# Revit family: Diverter_Trim-Grohe-Concetto-29102_Series
name_source: partatom
category: Plumbing Fixtures
units: mm (PartAtom-declared; Revit-internal decimal feet)

## family parameters
Cut with Voids When Loaded = No
Host = Face
OmniClass Number = 23.45.05.14.17
OmniClass Title = Showers
Part Type = Normal
Room Calculation Point = No
Round Connector Dimension = Use Diameter
Shared = Yes

## types (2) — shared parameters
ADA Compliant = No
Assembly Code = D2010710
CW Connection = Yes
CWFU = 1.5
Default Elevation = 40"
Description = CONCETTO Pressure Balance Valve Trim with Diverter
HW Connection = Yes
HWFU = 1.5
Height = 7 7/16"
Installation Type = Wall Mounted
Manufacturer = Grohe
Price = Prices may vary. Please consult Manufacturer Representative for most up-to-date price list.
Product Documentation Link = https://americanstandard.box.com
Product Page URL = https://www.grohe.us
Revised Date = 7/05/2021
Tempered Connection Diameter = 1/2"
Tempered Connection Radius = 1/4"
URL = https://www.grohe.com
Vent Connection = No
WFU = 2
Warranty Documentation Link = https://cdn.cloud.grohe.com
Waste Connection = No
Width = 7 7/16"

## per-type parameters (varying)
| type | Finish | Material |
| 29102001 | Metal-Grohe-001-Chrome | Metal-Grohe-001-Chrome |
| 29102EN1 | Metal-Grohe-EN1-Brushed Nickel | Metal-Grohe-EN1-Brushed Nickel |

note: column(s) folded — value = type name in every type: Model

## geometry (parser evidence)
native form markers: Sweep x5
no freeform markers — native parametric forms only
